# Revit family: EKF_EE_МонтажнаяПлатаFORT_PROxima
name_source: partatom
category: Электрооборудование
units: mm (PartAtom-declared; Revit-internal decimal feet)

## family parameters
Всегда вертикально = Нет
На основе рабочей плоскости = Да
Общий = Да
При загрузке вырезать с полостями = Нет
Размер круглого соединителя = Использовать диаметр
Тип детали = Силовой щит
Точка расчета площади = Нет

## types (11) — shared parameters
ADSK_Единица измерения = шт.
ADSK_Завод-изготовитель = EKF
ADSK_Количество = 1
ADSK_Марка = Монтажная панель FORT
ADSK_Материал = RAL 7035_Сталь
ADSK_Обозначение = Монтажная панель FORT
ADSK_Размер_Глубина = 2 мм
D = 6.5 мм
Изготовитель = EKF
КолОтв = 18
Отступ = 20 мм
Отступ2 = 21.5 мм
Серия номенклатуры = PROxima
Степень защиты IP = -
ТВ = EKF_2
Тип установки = -
zero-valued in all types: ADSK_Масса, Отметка по умолчанию

## per-type parameters (varying)
| type | ADSK_Код изделия | ADSK_Размер_Высота | ADSK_Размер_Ширина | b | h | Тип |
| Монтажная плата FORT для корпуса высотой 1800 и шириной 600 EKF PROxima | FM186 | 1800 мм | 600 мм | 524 мм | 1720 мм | 259 мм |
| Монтажная плата FORT для корпуса высотой 1800 и шириной 1000 EKF PROxima | FM1810 | 1800 мм | 1000 мм | 924 мм | 1720 мм | 258 мм |
| Монтажная плата FORT для корпуса высотой 1800 и шириной 800 EKF PROxima | FM188 | 1800 мм | 800 мм | 724 мм | 1720 мм | 260 мм |
| Монтажная плата FORT для корпуса высотой 2000 и шириной 1000 EKF PROxima | FM2010 | 2000 мм | 1000 мм | 924 мм | 1920 мм | 261 мм |
| Монтажная плата FORT для корпуса высотой 2000 и шириной 400 EKF PROxima | FM204 | 2000 мм | 400 мм | 324 мм | 1920 мм | 262 мм |
| Монтажная плата FORT для корпуса высотой 2000 и шириной 600 EKF PROxima | FM206 | 2000 мм | 600 мм | 524 мм | 1920 мм | 263 мм |
| Монтажная плата FORT для корпуса высотой 2000 и шириной 800 EKF PROxima | FM208 | 2000 мм | 800 мм | 724 мм | 1920 мм | 264 мм |
| Монтажная плата FORT для корпуса высотой 2200 и шириной 1000 EKF PROxima | FM2210 | 2200 мм | 1000 мм | 924 мм | 2120 мм | 265 мм |
| Монтажная плата FORT для корпуса высотой 2200 и шириной 400 EKF PROxima | FM224 | 2200 мм | 400 мм | 324 мм | 2120 мм | 266 мм |
| Монтажная плата FORT для корпуса высотой 2200 и шириной 600 EKF PROxima | FM226 | 2200 мм | 600 мм | 524 мм | 2120 мм | 267 мм |
| Монтажная плата FORT для корпуса высотой 2200 и шириной 800 EKF PROxima | FM228 | 2200 мм | 800 мм | 724 мм | 2120 мм | 268 мм |

note: column(s) folded — value = type name in every type: ADSK_Наименование
